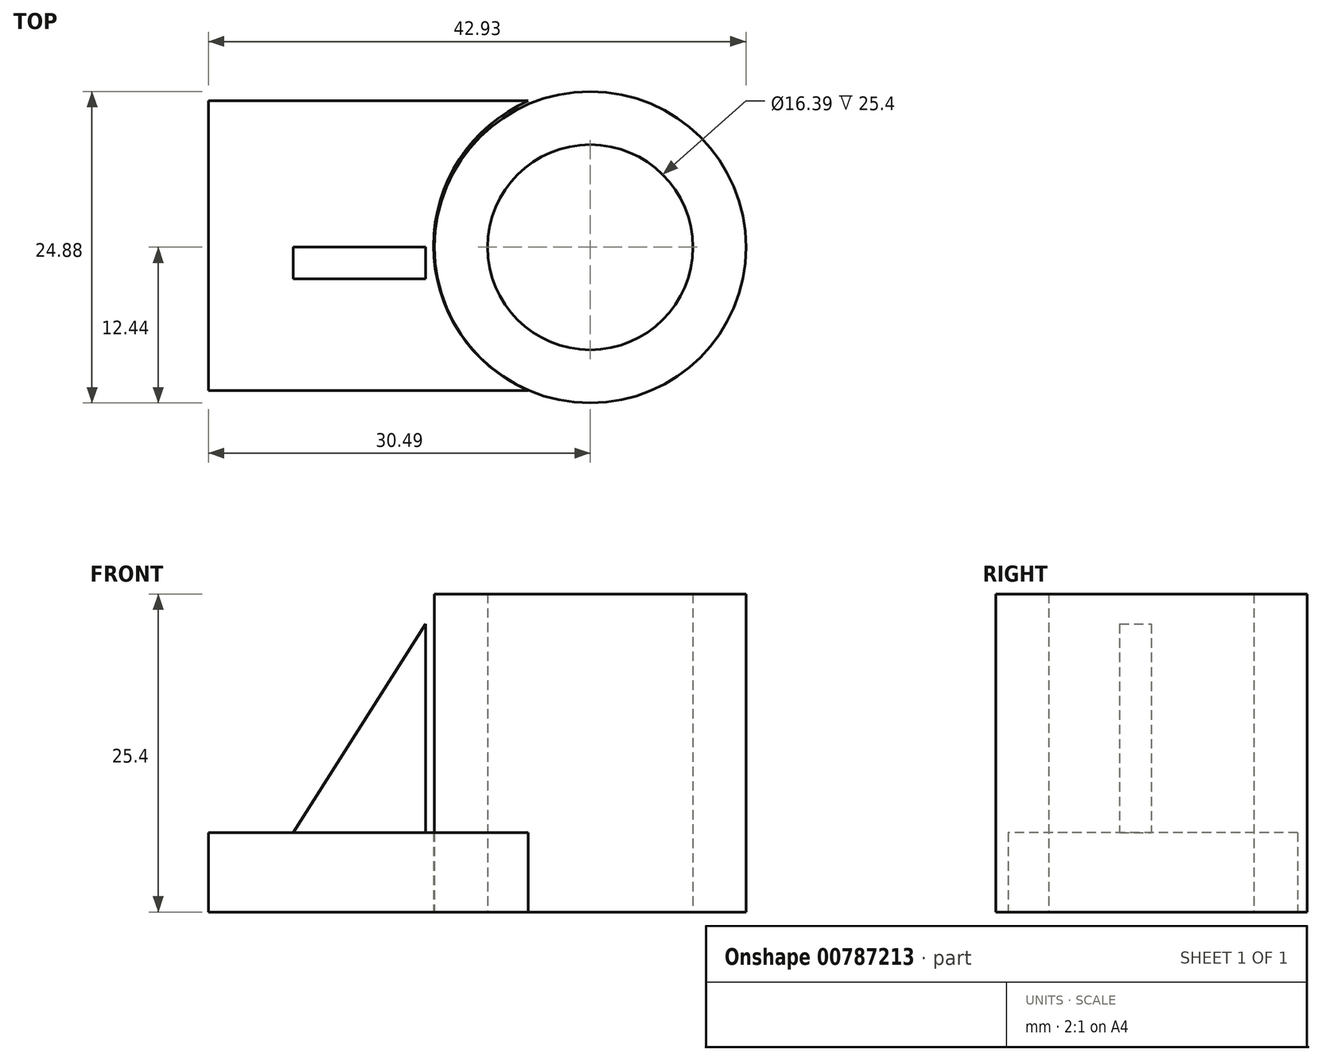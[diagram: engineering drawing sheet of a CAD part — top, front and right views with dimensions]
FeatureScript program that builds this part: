
annotation { "Feature Type Name" : "Feature", "Feature Type Description" : "" }
export const myFeature = defineFeature(function(context is Context, id is Id, definition is map)
    precondition{}
    {
        {
            var Q0;
            Q0=qCreatedBy(makeId("Top.planeOp"),FACE);
            var sketch = newSketch(context, id + "F0", { "sketchPlane" : qUnion([Q0])});
            skCircle(sketch, "E0", {"center": v(0, 0) * mm, "radius": 8.2 * mm});
            skCircle(sketch, "E1", {"center": v(0, 0) * mm, "radius": 12.44 * mm});
            skLineSegment(sketch, "E2.bottom", {"start": v(-4.52, 11.6) * mm, "end": v(-30.24, 11.6) * mm});
            skLineSegment(sketch, "E2.top", {"start": v(-4.52, -11.69) * mm, "end": v(-30.24, -11.69) * mm});
            skLineSegment(sketch, "E2.right", {"start": v(-30.24, 11.6) * mm, "end": v(-30.24, -11.69) * mm});
            skSolve(sketch);
        }
        {
            var Q0;
            Q0=makeQuery(id+"F0.imprint","IMPRINT",FACE,{"disambiguationData":[TD([[makeQuery(id+"F0.imprint","IMPRINT",EDGE,{"derivedFrom":sQuery(id+"F0.wireOp",EDGE,"E0")}),-1.0]])]});
            extrude(context, id + "F1", {"entities" : qUnion([Q0]), "depth" : 25.4 * mm, "offsetDistance" : 25.4 * mm});
        }
        {
            var Q0;
            Q0=qCreatedBy(makeId("Top.planeOp"),FACE);
            var sketch = newSketch(context, id + "F2", { "sketchPlane" : qUnion([Q0])});
            skLineSegment(sketch, "E3", {"start": v(-4.94, 11.69) * mm, "end": v(-30.49, 11.69) * mm});
            skLineSegment(sketch, "E4", {"start": v(-30.49, 11.69) * mm, "end": v(-30.49, -11.45) * mm});
            skLineSegment(sketch, "E5", {"start": v(-30.49, -11.45) * mm, "end": v(-4.94, -11.45) * mm});
            skArc(sketch, "E6", {"start": v(-4.94, 11.69) * mm, "mid": v(-12.5, 0.12) * mm, "end": v(-4.94, -11.45) * mm});
            skSolve(sketch);
        }
        {
            var Q0;
            Q0 = qSketchRegion(id + "F2", true);
            extrude(context, id + "F3", {"entities" : qUnion([Q0]), "depth" : 6.35 * mm, "offsetDistance" : 25.4 * mm});
        }
        {
            var Q0;
            Q0=qCreatedBy(makeId("Front.planeOp"),FACE);
            var sketch = newSketch(context, id + "F4", { "sketchPlane" : qUnion([Q0])});
            skLineSegment(sketch, "E7", {"start": v(-23.74, 6.3) * mm, "end": v(-13.13, 6.3) * mm});
            skLineSegment(sketch, "E8", {"start": v(-13.13, 6.3) * mm, "end": v(-13.13, 23) * mm});
            skLineSegment(sketch, "E9", {"start": v(-13.13, 23) * mm, "end": v(-23.74, 6.3) * mm});
            skSolve(sketch);
        }
        {
            var Q0;
            Q0 = qSketchRegion(id + "F4", true);
            extrude(context, id + "F5", {"entities" : qUnion([Q0]), "operationType" : NewBodyOperationType.ADD, "depth" : 2.54 * mm, "offsetDistance" : 25.4 * mm});
        }
    });
